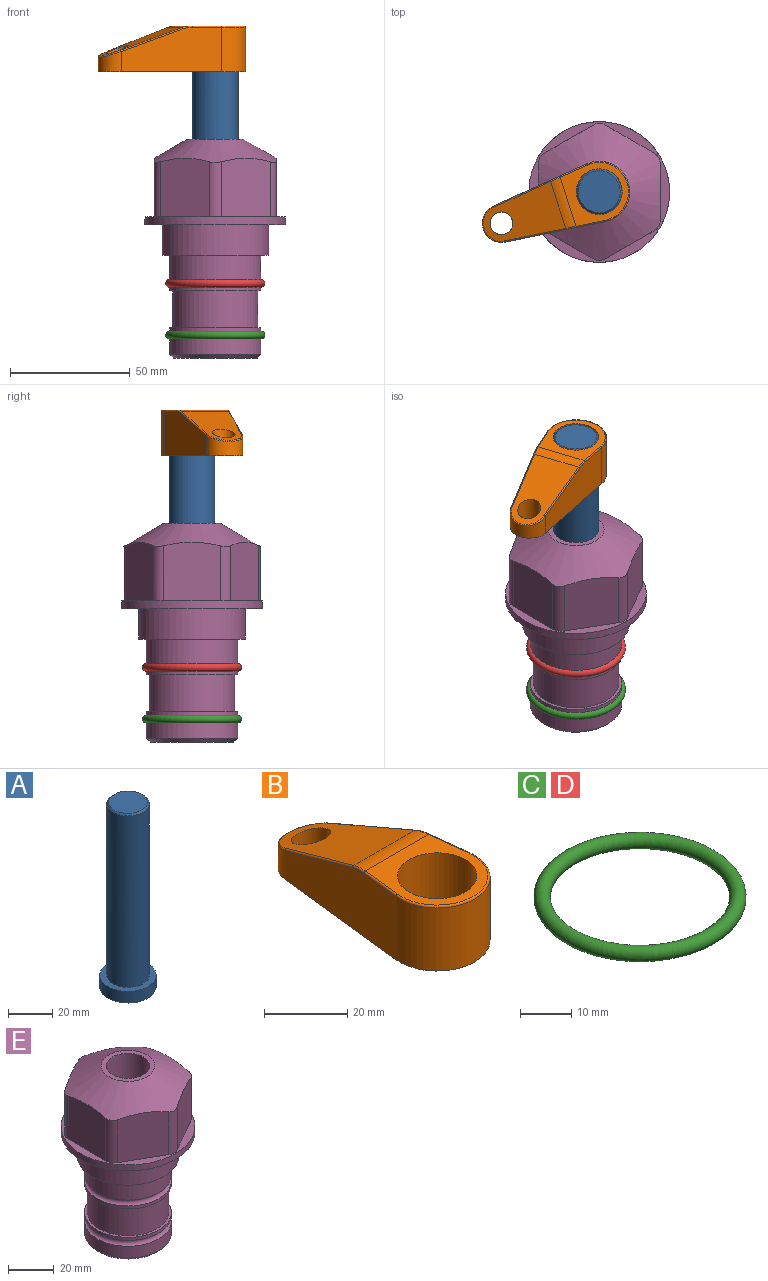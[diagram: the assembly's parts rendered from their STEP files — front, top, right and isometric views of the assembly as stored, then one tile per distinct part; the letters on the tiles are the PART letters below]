
ASSEMBLY  parts=5 mates=3
PART A: 6 faces, bbox 25.4x25.4x101.6 mm
  f0: plane 17.46x17.46mm, normal (0,0,1), area 239.5mm2, adj f5
  f1: plane 25.4x25.4mm, normal (0,0,-1), area 506.7mm2, adj f2
  f2: cylinder r=12.7mm len=25.4mm, axis (0,0,1), area 506.7mm2, adj f1,f3
  f3: plane 25.4x25.4mm, normal (0,0,1), area 221.7mm2, adj f2,f4
  f4: cylinder r=9.53mm len=94.46mm, axis (0,0,1), area 5653mm2, adj f3,f5
  f5: cone r=8.73mm half-angle=45deg, axis (0,0,-1), area 64.4mm2, adj f0,f4
PART B: 44 faces, bbox 27.5x64.5x19.1 mm
  f0: plane 2.3x0.95mm, normal (0,0,-1), area 1mm2, adj f25,f30,f34
  f1: plane 63.5x25.4mm, normal (0,0,-1), area 561.7mm2, adj f2,f3,f4,f5,f6,f7,f19,f20
  f2: cylinder r=12.7mm len=25.4mm, axis (0,0,-1), area 792.2mm2, adj f1,f3,f5,f13
  f3: plane 42.33x18.54mm, normal (0.99,0.11,0), area 647mm2, adj f1,f2,f4,f11,f12,f14
  f4: cylinder r=7.94mm len=15.78mm, axis (0,0,-1), area 158.6mm2, adj f1,f3,f5,f16
  f5: plane 42.33x18.54mm, normal (-0.99,0.11,0), area 647mm2, adj f1,f2,f4,f15,f17,f18
  f6: cylinder r=9.53mm len=19.05mm, axis (0,0,-1), area 1140.1mm2, adj f1,f8
  f7: cylinder r=4.76mm len=10.98mm, axis (0,0,-1), area 276.1mm2, adj f1,f9
  f8: plane 25.83x24.38mm, normal (0,0,1), area 262.2mm2, adj f6,f10,f11,f13,f15
  f9: plane 32.49x20.55mm, normal (0,0.34,0.94), area 489.9mm2, adj f7,f10,f14,f16,f18
  f10: cylinder r=12.7mm len=21.49mm, axis (-1,0,0), area 93.2mm2, adj f8,f9,f12,f17
  f11: cylinder r=0.51mm len=12.34mm, axis (0.11,-0.99,0), area 9.9mm2, adj f3,f8,f12,f13
  f12: bspline ~7.62x1.64mm, area 3.5mm2, adj f3,f10,f11,f14
  f13: torus R=12.19mm, axis (0,0,1), area 33.6mm2, adj f2,f8,f11,f15
  f14: cylinder r=0.51mm len=26.01mm, axis (0.1,-0.93,0.34), area 21.6mm2, adj f3,f9,f12,f16
  f15: cylinder r=0.51mm len=12.34mm, axis (0.11,0.99,0), area 9.9mm2, adj f5,f8,f13,f17
  f16: bspline ~15.78x7.05mm, area 15.7mm2, adj f4,f9,f14,f18
  f17: bspline ~7.62x1.64mm, area 3.5mm2, adj f5,f10,f15,f18
  f18: cylinder r=0.51mm len=26.01mm, axis (0.1,0.93,-0.34), area 21.6mm2, adj f5,f9,f16,f17
  f19: plane 21.6x14.29mm, normal (-0.99,-0.11,0), area 242.6mm2, adj f1,f26,f28,f34,f36,f38
  f20: plane 21.6x14.29mm, normal (0.99,-0.11,0), area 242.6mm2, adj f1,f27,f29,f37,f39,f41
  f21: cylinder r=12.7mm len=14.29mm, axis (0,0,-1), area 173.2mm2, adj f1,f26,f27,f30,f31,f33
  f22: cylinder r=7.94mm len=7.63mm, axis (0,0,-1), area 53.8mm2, adj f1,f28,f29,f42
  f23: plane 2.3x0.95mm, normal (0,0,-1), area 1mm2, adj f25,f33,f37
  f24: plane 17.94x12.32mm, normal (0,-0.34,-0.94), area 191.2mm2, adj f25,f38,f41,f42
  f25: cylinder r=9.53mm len=12.93mm, axis (-1,0,0), area 37.5mm2, adj f0,f23,f24,f31,f36,f39
  f26: cylinder r=1.59mm len=14.29mm, axis (0,0,-1), area 49mm2, adj f1,f19,f21,f32
  f27: cylinder r=1.59mm len=14.29mm, axis (0,0,-1), area 49mm2, adj f1,f20,f21,f35
  f28: cylinder r=1.59mm len=7.28mm, axis (0,0,-1), area 22.1mm2, adj f1,f19,f22,f40
  f29: cylinder r=1.59mm len=7.28mm, axis (0,0,-1), area 22.1mm2, adj f1,f20,f22,f43
  f30: torus R=14.29mm, axis (0,0,1), area 5.8mm2, adj f0,f21,f31,f32
  f31: bspline ~11.06x2.73mm, area 20.8mm2, adj f21,f25,f30,f33
  f32: sphere r=1.59mm, area 5.4mm2, adj f26,f30,f34
  f33: torus R=14.29mm, axis (0,0,1), area 5.8mm2, adj f21,f23,f31,f35
  f34: cylinder r=1.59mm len=1.68mm, axis (-0.11,0.99,0), area 2.4mm2, adj f0,f19,f32,f36
  f35: sphere r=1.59mm, area 5.4mm2, adj f27,f33,f37
  f36: bspline ~5.82x2.33mm, area 7.7mm2, adj f19,f25,f34,f38
  f37: cylinder r=1.59mm len=1.68mm, axis (0.11,0.99,0), area 2.4mm2, adj f20,f23,f35,f39
  f38: cylinder r=1.59mm len=18.33mm, axis (0.1,-0.93,0.34), area 46.7mm2, adj f19,f24,f36,f40
  f39: bspline ~5.82x2.33mm, area 7.7mm2, adj f20,f25,f37,f41
  f40: sphere r=1.59mm, area 3.6mm2, adj f28,f38,f42
  f41: cylinder r=1.59mm len=18.33mm, axis (0.1,0.93,-0.34), area 46.7mm2, adj f20,f24,f39,f43
  f42: bspline ~8.31x1.84mm, area 15.3mm2, adj f22,f24,f40,f43
  f43: sphere r=1.59mm, area 3.6mm2, adj f29,f41,f42
PART C: 1 faces, bbox 44.7x44.7x3.2 mm
  f0: torus R=19.05mm, axis (0,0,1), area 1193.9mm2
PART D: same geometry as C
PART E: 36 faces, bbox 58.7x58.7x91.2 mm
  f0: cylinder r=17.78mm len=35.56mm, axis (0,0,1), area 1670.8mm2, adj f23,f24,f31
  f1: cylinder r=19.05mm len=38.1mm, axis (0,0,1), area 1191.9mm2, adj f26,f27,f30
  f2: plane 58.66x58.66mm, normal (0,0,-1), area 1150.6mm2, adj f3,f28
  f3: cylinder r=29.33mm len=58.66mm, axis (0,0,-1), area 585.1mm2, adj f2,f4
  f4: plane 58.66x58.66mm, normal (0,0,1), area 475.9mm2, adj f3,f5,f6,f7,f8,f9,f10,f11
  f5: plane 24.5x20.32mm, normal (-0.5,0.87,0), area 562.8mm2, adj f4,f15,f16,f17
  f6: plane 24.5x20.32mm, normal (0.5,0.87,0), area 562.8mm2, adj f4,f14,f15,f17
  f7: plane 24.5x23.48mm, normal (1,0,0), area 562.8mm2, adj f4,f13,f14,f17
  f8: plane 24.5x20.32mm, normal (0.5,-0.87,0), area 562.8mm2, adj f4,f12,f13,f17
  f9: plane 24.5x20.32mm, normal (-0.5,-0.87,0), area 562.8mm2, adj f4,f11,f12,f17
  f10: plane 24.5x23.48mm, normal (-1,0,0), area 562.8mm2, adj f4,f11,f16,f17
  f11: cylinder r=5.08mm len=23.01mm, axis (0,0,-1), area 121.2mm2, adj f4,f9,f10,f17
  f12: cylinder r=5.08mm len=23.01mm, axis (0,0,-1), area 121.2mm2, adj f4,f8,f9,f17
  f13: cylinder r=5.08mm len=23.01mm, axis (0,0,-1), area 121.2mm2, adj f4,f7,f8,f17
  f14: cylinder r=5.08mm len=23.01mm, axis (0,0,-1), area 121.2mm2, adj f4,f6,f7,f17
  f15: cylinder r=5.08mm len=23.01mm, axis (0,0,-1), area 121.2mm2, adj f4,f5,f6,f17
  f16: cylinder r=5.08mm len=23.01mm, axis (0,0,-1), area 121.2mm2, adj f4,f5,f10,f17
  f17: cone r=11.73mm half-angle=60deg, axis (0,0,-1), area 2071.8mm2, adj f5,f6,f7,f8,f9,f10,f11,f12
  f18: plane 23.46x23.46mm, normal (0,0,1), area 147.4mm2, adj f17,f35
  f19: plane 34.93x34.93mm, normal (0,0,-1), area 958mm2, adj f29
  f20: cylinder r=19.05mm len=38.1mm, axis (0,0,1), area 760.1mm2, adj f21,f29
  f21: torus R=19.05mm, axis (0,0,1), area 565.3mm2, adj f20,f22
  f22: cylinder r=19.05mm len=38.1mm, axis (0,0,1), area 190mm2, adj f21,f23
  f23: plane 38.1x38.1mm, normal (0,0,1), area 146.9mm2, adj f0,f22
  f24: plane 38.1x38.1mm, normal (0,0,-1), area 146.9mm2, adj f0,f25
  f25: cylinder r=19.05mm len=38.1mm, axis (0,0,1), area 190mm2, adj f24,f26
  f26: torus R=19.05mm, axis (0,0,1), area 565.3mm2, adj f1,f25
  f27: plane 44.45x44.45mm, normal (0,0,-1), area 411.7mm2, adj f1,f28
  f28: cylinder r=22.23mm len=44.45mm, axis (0,0,1), area 1773.5mm2, adj f2,f27
  f29: cone r=19.05mm half-angle=45deg, axis (0,0,1), area 257.5mm2, adj f19,f20
  f30: cylinder r=3.17mm len=6.75mm, axis (-1,0,0), area 128mm2, adj f1,f33
  f31: cylinder r=3.17mm len=6.35mm, axis (-1,0,0), area 102.5mm2, adj f0,f33
  f32: plane 25.4x25.4mm, normal (0,0,1), area 506.7mm2, adj f33
  f33: cylinder r=12.7mm len=66.42mm, axis (0,0,-1), area 5236.2mm2, adj f30,f31,f32,f34
  f34: cone r=9.53mm half-angle=30deg, axis (0,0,-1), area 443.4mm2, adj f33,f35
  f35: cylinder r=9.53mm len=19.05mm, axis (0,0,-1), area 849mm2, adj f18,f34
PLACE A rot(axis=(0,0,-1),162.1deg) t=(0,0,9.12)mm
PLACE B rot(axis=(0,0,1),107.9deg) t=(0,0,63.73)mm
PLACE C t=(0,0,-21.59)mm
PLACE D at identity
PLACE E at identity fixed
MATE fastened C.f0 <-> E.f0  axis (0,0,1) through (0,0,-46.1)mm
MATE cylindrical A.f2 <-> E.f0  axis (0,0,1) through (0,0,34.76)mm
MATE fastened B.f2 <-> A.f2  axis (0,0,1) through (0,0,82.78)mm
